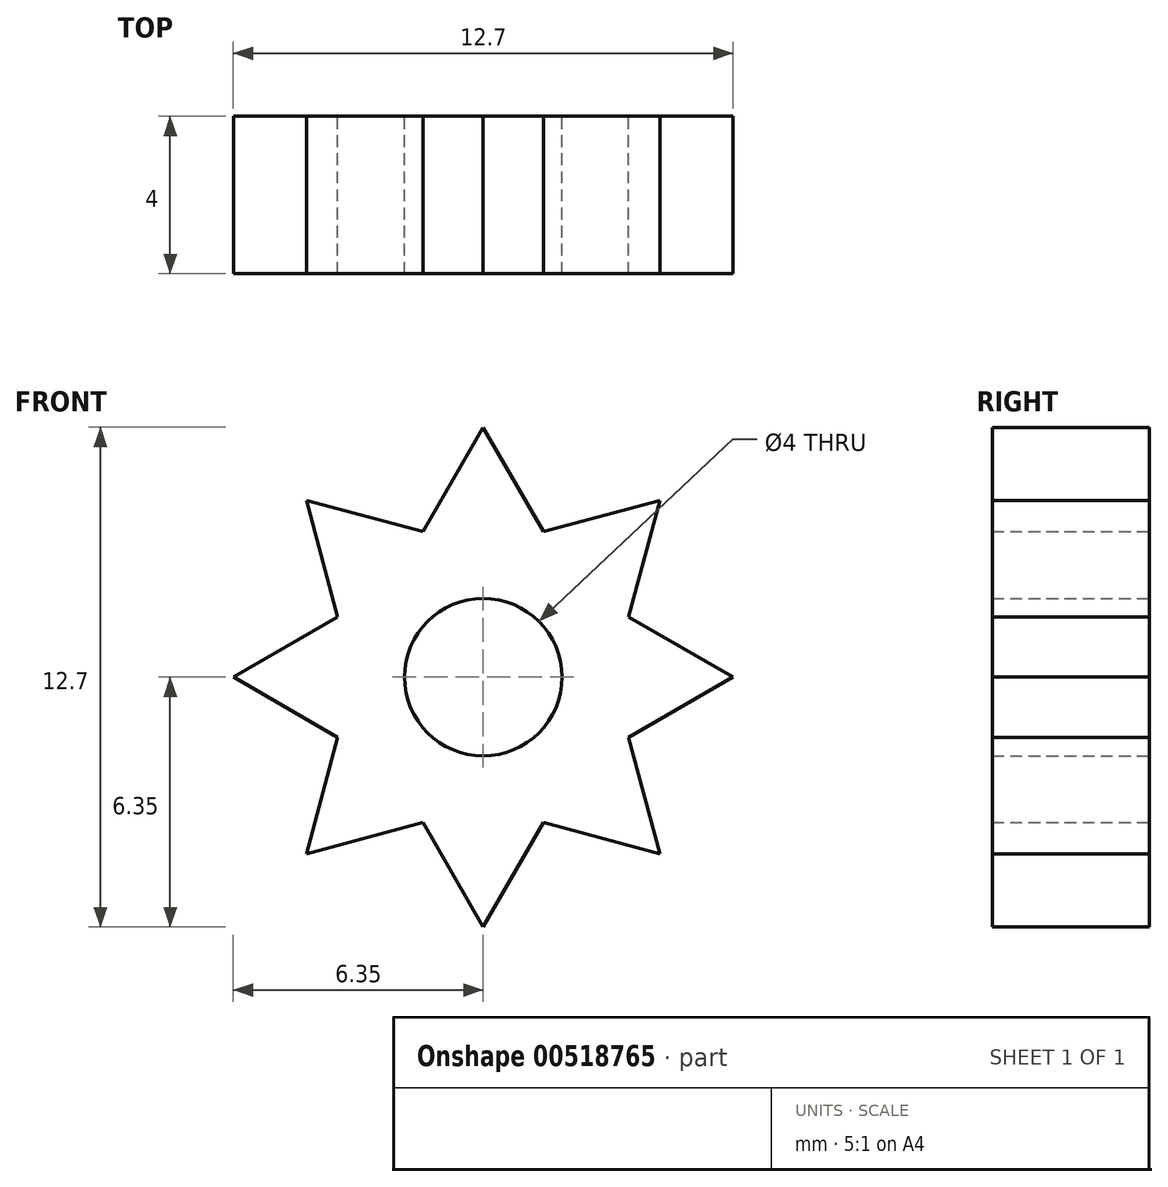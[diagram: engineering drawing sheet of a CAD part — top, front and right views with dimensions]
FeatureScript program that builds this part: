
annotation { "Feature Type Name" : "Feature", "Feature Type Description" : "" }
export const myFeature = defineFeature(function(context is Context, id is Id, definition is map)
    precondition{}
    {
        {
            var Q0;
            Q0=qCreatedBy(makeId("Front.planeOp"),FACE);
            var sketch = newSketch(context, id + "F0", { "sketchPlane" : qUnion([Q0])});
            skCircle(sketch, "E0", {"center": v(0, 0) * mm, "radius": 4 * mm});
            skCircle(sketch, "E1", {"center": v(0, 0) * mm, "radius": 2 * mm});
            skLineSegment(sketch, "E2", {"start": v(0, 0) * mm, "end": v(-1.53, 3.7) * mm, "construction": true});
            skLineSegment(sketch, "E3", {"start": v(-1.53, 3.7) * mm, "end": v(0, 6.35) * mm});
            skLineSegment(sketch, "E4", {"start": v(0, 6.35) * mm, "end": v(1.53, 3.7) * mm});
            skLineSegment(sketch, "E5.1.0", {"start": v(-3.7, 1.53) * mm, "end": v(-4.49, 4.49) * mm});
            skLineSegment(sketch, "E5.1.1", {"start": v(-4.49, 4.49) * mm, "end": v(-1.53, 3.7) * mm});
            skLineSegment(sketch, "E5.2.0", {"start": v(-3.7, -1.53) * mm, "end": v(-6.35, 0) * mm});
            skLineSegment(sketch, "E5.2.1", {"start": v(-6.35, 0) * mm, "end": v(-3.7, 1.53) * mm});
            skLineSegment(sketch, "E5.3.0", {"start": v(-1.53, -3.7) * mm, "end": v(-4.49, -4.49) * mm});
            skLineSegment(sketch, "E5.3.1", {"start": v(-4.49, -4.49) * mm, "end": v(-3.7, -1.53) * mm});
            skLineSegment(sketch, "E5.4.0", {"start": v(1.53, -3.7) * mm, "end": v(0, -6.35) * mm});
            skLineSegment(sketch, "E5.4.1", {"start": v(0, -6.35) * mm, "end": v(-1.53, -3.7) * mm});
            skLineSegment(sketch, "E5.5.0", {"start": v(3.7, -1.53) * mm, "end": v(4.49, -4.49) * mm});
            skLineSegment(sketch, "E5.5.1", {"start": v(4.49, -4.49) * mm, "end": v(1.53, -3.7) * mm});
            skLineSegment(sketch, "E5.6.0", {"start": v(3.7, 1.53) * mm, "end": v(6.35, 0) * mm});
            skLineSegment(sketch, "E5.6.1", {"start": v(6.35, 0) * mm, "end": v(3.7, -1.53) * mm});
            skLineSegment(sketch, "E5.7.0", {"start": v(1.53, 3.7) * mm, "end": v(4.49, 4.49) * mm});
            skLineSegment(sketch, "E5.7.1", {"start": v(4.49, 4.49) * mm, "end": v(3.7, 1.53) * mm});
            skSolve(sketch);
        }
        {
            var Q0;
            Q0 = qSketchRegion(id + "F0", true);
            extrude(context, id + "F1", {"entities" : qUnion([Q0]), "endBound" : BoundingType.SYMMETRIC, "depth" : 4 * mm, "offsetDistance" : 25 * mm});
        }
    });
